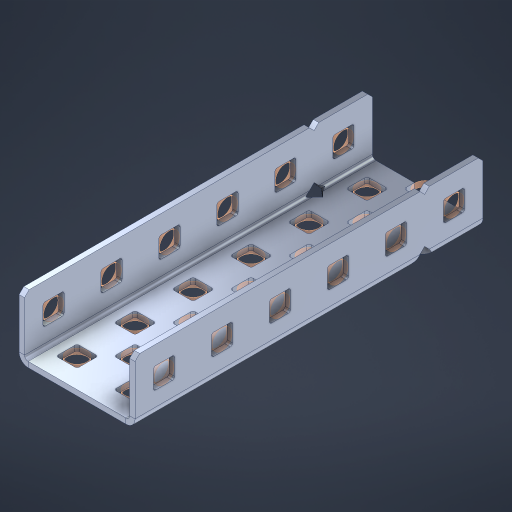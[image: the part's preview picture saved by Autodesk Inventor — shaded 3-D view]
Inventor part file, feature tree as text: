
AUTODESK INVENTOR PART (.ipt)
format: ipt  version: 2023 (Build 270158000, 158)  size: 732,160 bytes
history: native  units: in
note: dims shown in document units (in); Inventor stores cm internally (conversion verified against a paired STEP export)
features: other x37, extrude x28, sheet_metal_op x11, sketch x10, pattern_linear x2, mirror x1, chamfer x1
ambient origin geometry x8: Origin, YZ Plane, XZ Plane, XY Plane, X Axis, Y Axis, Z Axis, Center Point
bodies: Solid1 (feature_tree), Body (feature_tree)
feature tree (90):
  sheet_metal_op  "Flanges"
  other  "Flange Pattern Plane"
  other  "Flange Pattern Sketch"
  sheet_metal_op  "Flange Pattern"
  sheet_metal_op  "Body Pattern"
  pattern_linear  "Center Pattern"  Spacing1=0.0469in  [1 undecoded]
  other  "Arc Length"
  mirror  "Notch Mirror"
  pattern_linear  "Notch Pattern"  Spacing1=0.182in  [1 undecoded]
  chamfer  "End Chamfer"
  extrude  "Half Cut"  Depth=0.02in
  sketch  "Sketch1"  dims[d0=1.0in]
  other  "Plate1"
  sketch  "Sketch2"  dims[d1=3.0in]
  other  "Plate2"
  sheet_metal_op  "Bend1"
  sheet_metal_op  "Corner1"
  sketch  "Sketch3"  dims[d2=0.0469in]
  sketch  "Sketch7"  dims[d3=0.0469in]
  other  "Srf1"
  other  "Srf2"
  sketch  "Sketch8"  dims[d4=0.0234in]
  sketch  "Sketch9"  dims[d5=0.0938in]
  other  "Srf91"
  sheet_metal_op  "Body Pattern Sketch"
  other  "Srf92"
  sketch  "Sketch13"  dims[d6=0.0469in]
  sketch  "Sketch14"  dims[d7=0.5in d8=90.0deg d9=0.0312in]
  sketch  "Sketch15"  dims[d10=0.1875in]
  sketch  "Sketch16"  dims[d11=0.0469in d12=0.0469in d16=0.182in d17=0.02in d18=0.0469in d19=0.0in d20=0.25in d21=0.25in d38=2.3622in d40=0.5in d41=0.7874in d43=1.0in d46=0.172in d47=1.0in d48=0.0in d49=0.182in d50=0.02in d51=0.25in d52=0.25in d53=0.0469in d54=0.0in d55=0.172in d56=1.0in d57=0.0in d58=0.25in d60=2.3622in d62=0.5in d63=0.7874in d65=0.5in d85=0.1227in d86=0.1659in d88=0.04in d89=0.0469in d90=0.0in d91=0.04in d92=0.0491in d95=2.5in d96=0.04in d97=0.25in d98=45.0deg d99=0.25in d100=0.5in d101=0.0in d102=2.497in d106=0.182in d107=0.02in d108=0.5in d109=0.5in d110=0.0469in d111=0.0in d112=0.172in d113=0.5in d114=0.0in d117=0.5in d118=0.5in d119=0.5in]
  other  "Srf786"
  other  "Srf823"
  other  "Srf824"
  other  "Srf825"
  other  "Srf826"
  other  "Srf827"
  other  "Srf828"
  other  "Srf829"
  other  "Srf856"
  other  "Srf857"
  other  "Srf858"
  other  "Srf859"
  other  "Srf860"
  other  "Srf861"
  other  "Srf862"
  other  "Srf889"
  other  "Srf890"
  other  "Srf891"
  other  "Srf892"
  other  "Srf893"
  other  "Srf922"
  other  "Srf923"
  other  "Srf924"
  other  "Srf959"
  other  "Srf960"
  other  "Srf961"
  sheet_metal_op  "Flange Stamp"
  sheet_metal_op  "Flange Circle"
  sheet_metal_op  "Body Stamp"
  sheet_metal_op  "Body Circle"
  other  "Center Stamp"
  other  "Center Circle"
  sheet_metal_op  "Notch"
  extrude  "ExtrusionSrf2"  Depth=0.0469in
  extrude  "ExtrusionSrf92"  TaperAngle=0.0deg  [1 undecoded]
  extrude  "ExtrusionSrf823"  Depth=0.5in
  extrude  "ExtrusionSrf824"  Depth=0.5in
  extrude  "ExtrusionSrf825"  Depth=0.5in
  extrude  "ExtrusionSrf826"  Depth=0.5in
  extrude  "ExtrusionSrf827"  Depth=1.0in TaperAngle=0.0deg
  extrude  "ExtrusionSrf828"  Depth=0.5in
  extrude  "ExtrusionSrf829"  Depth=0.02in
  extrude  "ExtrusionSrf856"  Depth=0.5in
  extrude  "ExtrusionSrf857"  Depth=0.5in
  extrude  "ExtrusionSrf858"  Depth=0.0469in
  extrude  "ExtrusionSrf859"  TaperAngle=0.0deg  [1 undecoded]
  extrude  "ExtrusionSrf860"  Depth=0.5in
  extrude  "ExtrusionSrf861"  Depth=1.0in TaperAngle=0.0deg
  extrude  "ExtrusionSrf862"  Depth=0.5in
  extrude  "ExtrusionSrf889"  Depth=0.5in
  extrude  "ExtrusionSrf890"  Depth=0.5in
  extrude  "ExtrusionSrf891"  Depth=0.5in
  extrude  "ExtrusionSrf892"  Depth=0.5in
  extrude  "ExtrusionSrf893"  Depth=0.5in
  extrude  "ExtrusionSrf922"  Depth=0.0469in
  extrude  "ExtrusionSrf923"  TaperAngle=0.0deg  [1 undecoded]
  extrude  "ExtrusionSrf924"  Depth=0.5in
  extrude  "ExtrusionSrf959"  Depth=0.5in
  extrude  "ExtrusionSrf960"  Depth=2.5in
  extrude  "ExtrusionSrf961"  Depth=0.5in TaperAngle=45.0deg
note: 5 required parameter values undecoded (feature->parameter linkage not recoverable at this tier; creation-order binding heuristic only, values carry confidence <= 0.55)
